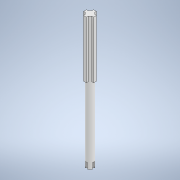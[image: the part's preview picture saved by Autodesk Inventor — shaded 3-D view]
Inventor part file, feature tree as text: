
AUTODESK INVENTOR PART (.ipt)
format: ipt  version: 2022 (Build 260153000, 153)  size: 167,424 bytes
history: native  units: in
note: dims shown in document units (in); Inventor stores cm internally (conversion verified against a paired STEP export)
features: extrude x3, sketch x3
ambient origin geometry x8: Origin, YZ Plane, XZ Plane, XY Plane, X Axis, Y Axis, Z Axis, Center Point
bodies: Body1 (feature_tree)
feature tree (6):
  extrude  "Extrusion7"  Depth=5.1181in TaperAngle=0.0deg
  extrude  "Extrusion8"  Depth=0.1181in
  extrude  "Extrusion9"  Depth=0.1181in
  sketch  "Sketch7"  dims[d71=0.2953in d72=5.1181in d73=0.0in]
  sketch  "Sketch8"  dims[d74=0.1181in d75=0.1181in]
  sketch  "Sketch9"  dims[d76=0.1181in d77=0.1181in d78=0.1181in d79=0.1181in d80=0.1181in d81=0.1181in d82=0.3937in d83=0.0in d84=1.9685in d85=0.0in d86=0.0787in d87=0.0787in d88=0.0787in d89=0.0787in d90=0.0787in d91=0.0787in d92=0.0787in d93=0.0787in d94=0.2362in d95=0.0in]
